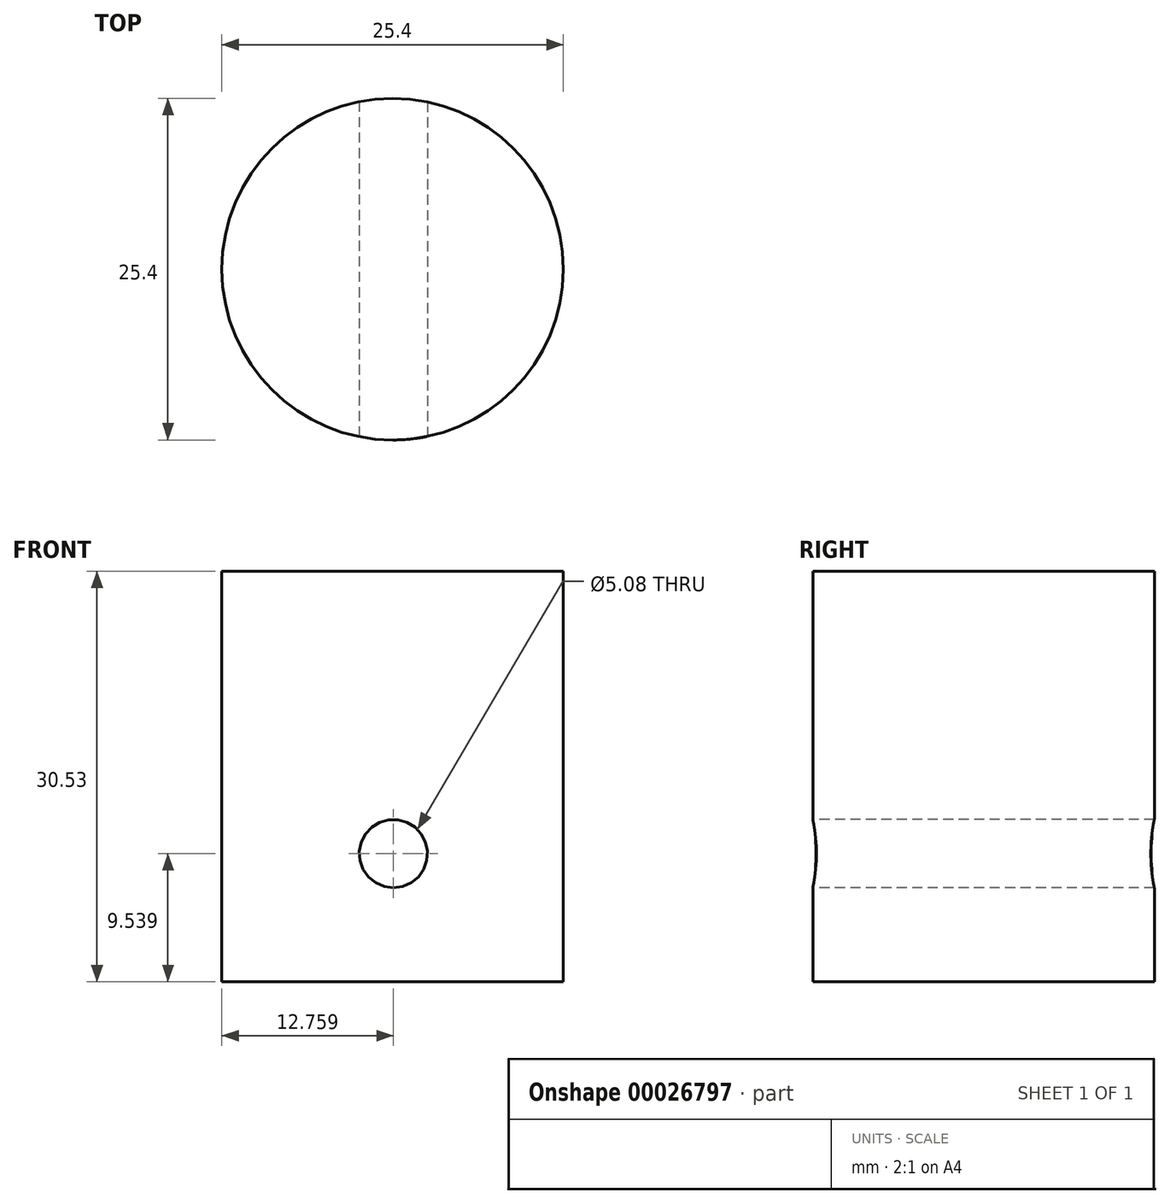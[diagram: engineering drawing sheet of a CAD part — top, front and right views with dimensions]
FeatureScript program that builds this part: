
annotation { "Feature Type Name" : "Feature", "Feature Type Description" : "" }
export const myFeature = defineFeature(function(context is Context, id is Id, definition is map)
    precondition{}
    {
        {
            var Q0;
            Q0=qCreatedBy(makeId("Top.planeOp"),FACE);
            var sketch = newSketch(context, id + "F0", { "sketchPlane" : qUnion([Q0])});
            skCircle(sketch, "E0", {"center": v(-46.05, 11.9) * mm, "radius": 12.7 * mm});
            skSolve(sketch);
        }
        {
            var Q0;
            Q0=makeQuery(id+"F0.imprint","IMPRINT",FACE,{"disambiguationData":[TD([[makeQuery(id+"F0.imprint","IMPRINT",EDGE,{"derivedFrom":sQuery(id+"F0.wireOp",EDGE,"E0")}),1.0]])]});
            extrude(context, id + "F1", {"entities" : qUnion([Q0]), "depth" : 30.53 * mm});
        }
        {
            var Q0;
            Q0=qCreatedBy(makeId("Front.planeOp"),FACE);
            var sketch = newSketch(context, id + "F2", { "sketchPlane" : qUnion([Q0])});
            skCircle(sketch, "E1", {"center": v(-46, 9.54) * mm, "radius": 2.54 * mm});
            skSolve(sketch);
        }
        {
            var Q0;
            Q0=makeQuery(id+"F2.imprint","IMPRINT",FACE,{"disambiguationData":[TD([[makeQuery(id+"F2.imprint","IMPRINT",EDGE,{"derivedFrom":sQuery(id+"F2.wireOp",EDGE,"E1")}),1.0]])]});
            extrude(context, id + "F3", {"entities" : qUnion([Q0]), "operationType" : NewBodyOperationType.REMOVE, "endBound" : BoundingType.SYMMETRIC, "oppositeDirection" : true, "depth" : 60.45 * mm});
        }
    });
